# Revit family: 2-5137-24 Balance_2x3 JBOX
name_source: partatom
category: Lighting Fixtures
revit_build: Autodesk Revit LT 2014 (Build: 20130308_1515(x64)
units: mm (PartAtom-declared; Revit-internal decimal feet)

## types (1)
- 2-5137-24 Balance_2x3 JBOX
    ADA Compliant = Yes
    Apparent Load = 26 VA
    Ballast Manufacturer = ANTRON
    Color Filter = 16777215
    Default Elevation = 4' - 0"
    Description = 24" Vanity - 1x T-5 linear fluorescent
    Diffuser = Acrylic - Matte White
    Dimming Lamp Color Temperature Shift = <None>
    Emit Shape Visible in Rendering = No
    Emit from Rectangle Length = 4' - 0"
    Emit from Rectangle Width = 2' - 0"
    Fixture Depth = 0' - 3 1/2"
    Fixture Height = 0' - 2 1/2"
    Fixture Length = 2' - 0 5/8"
    Input Power (Watts) = 25.80
    Input Voltage (VAC) = 120.0
    Junction Box = 2"x 3" or 4" Octogonal with accessory backplate
    Lamp = 1x24W T-5 Linear Fluorescent
    Lamp Manufacturer = Sylvania
    Manufacturer = Oxygen Lighting
    Metal Finish = Satin Nickel
    Model = 2-5137-24
    Optional Backplate = Yes
    Photometric Web File = 2-5137-24 Balance 24 ITL77178.IES
    Power Factor = 0.99
    Product Documentation Link = http://oxygenlighting.com.s3.amazonaws.com
    Tilt Angle = 180.00°
    Type Comments = Lighting
    URL = http://www.oxygenlighting.com

## geometry (parser evidence)
native form markers: Sweep x1
no freeform markers — native parametric forms only
